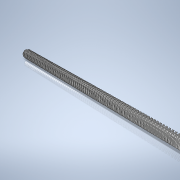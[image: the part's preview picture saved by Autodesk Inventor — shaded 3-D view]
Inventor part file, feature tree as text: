
AUTODESK INVENTOR PART (.ipt)
format: ipt  version: 2020.2 (Build 242310000, 310)  size: 1,128,448 bytes
history: native  units: mm
features: sketch x3, other x2, extrude x2
ambient origin geometry x8: Origin, YZ Plane, XZ Plane, XY Plane, X Axis, Y Axis, Z Axis, Center Point
bodies: Body1 (feature_tree)
feature tree (7):
  other  "Bryła1"
  extrude  "Wyciągnięcie proste1"  Depth=6.0mm
  other  "Zwój1"
  extrude  "Wyciągnięcie proste2"  Depth=150.0mm
  sketch  "Szkic1"
  sketch  "Szkic2"
  sketch  "Szkic3"
